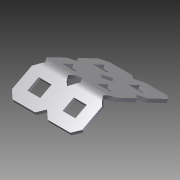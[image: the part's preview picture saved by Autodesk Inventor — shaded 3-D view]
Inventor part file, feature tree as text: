
AUTODESK INVENTOR PART (.ipt)
format: ipt  version: 2014 SP1 (Build 180222100, 222)  size: 573,952 bytes
history: native  units: in
note: dims shown in document units (in); Inventor stores cm internally (conversion verified against a paired STEP export)
features: other x2, sketch x2, imported_body x1, extrude x1
ambient origin geometry x8: Origin, YZ Plane, XZ Plane, XY Plane, X Axis, Y Axis, Z Axis, Center Point
bodies: Body1 (feature_tree)
feature tree (6):
  parser-record x1  (decoder bookkeeping rows leaked as tree rows — omitted from the tree; the rows remain in map.json)
  imported_body  "Base1"
  extrude  "Extrusion1"  Depth=1.5in
  other  "Bend Part2"
  sketch  "Sketch1"  dims[d0=1.0in d1=1.5in]
  sketch  "Sketch3"  dims[d2=1.0in d3=0.0in d8=0.5in d9=0.3779in d10=0.1in]
